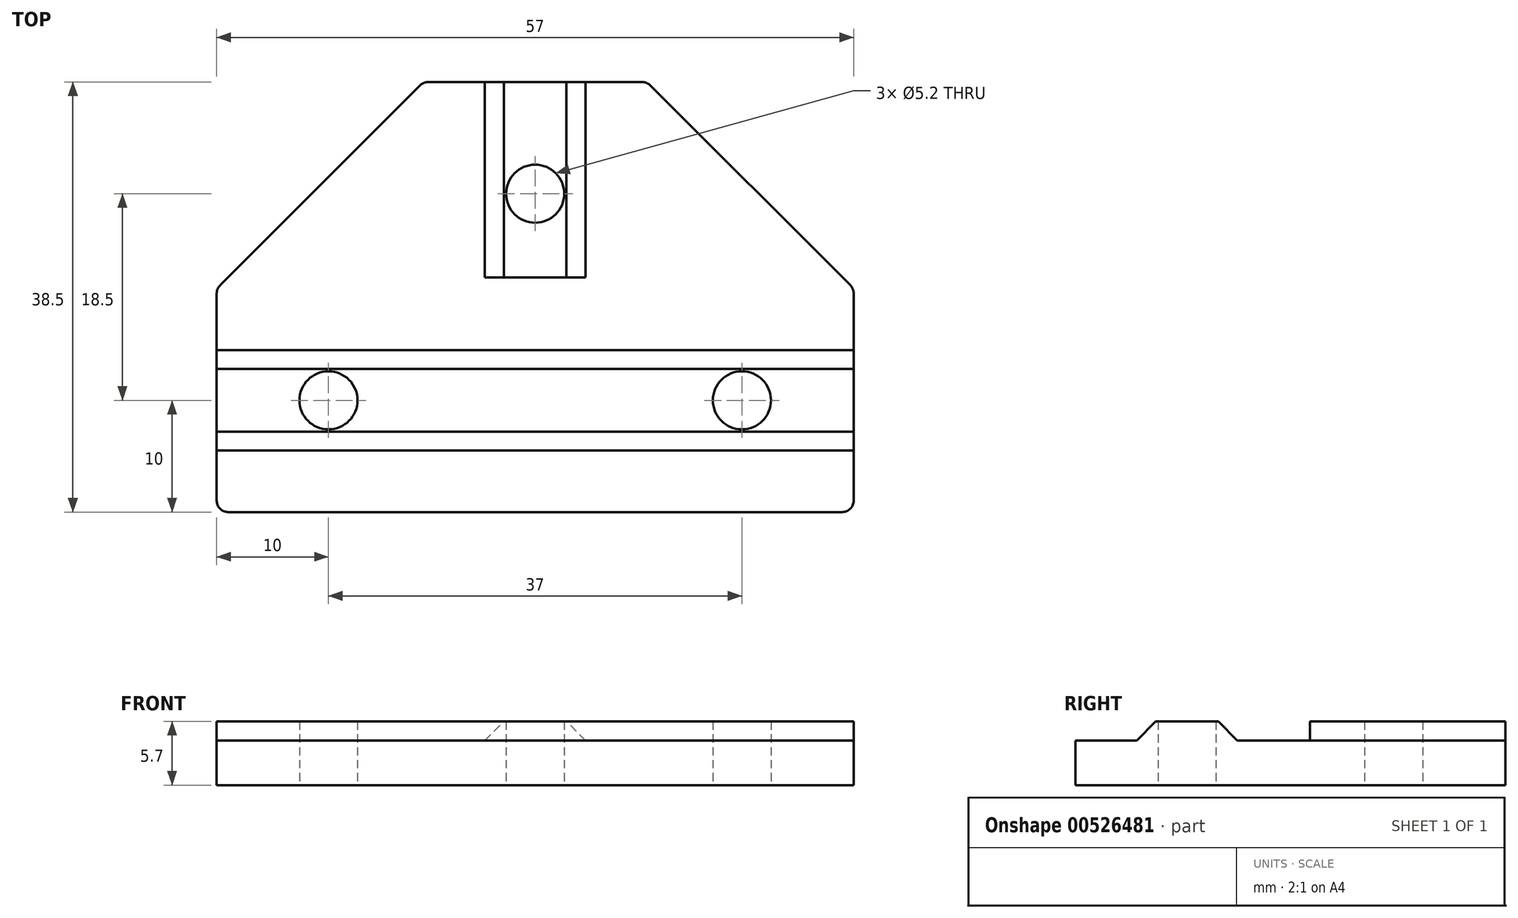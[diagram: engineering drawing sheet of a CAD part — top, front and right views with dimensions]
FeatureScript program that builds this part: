
annotation { "Feature Type Name" : "Feature", "Feature Type Description" : "" }
export const myFeature = defineFeature(function(context is Context, id is Id, definition is map)
    precondition{}
    {
        {
            var Q0;
            Q0=qCreatedBy(makeId("Top.planeOp"),FACE);
            var sketch = newSketch(context, id + "F0", { "sketchPlane" : qUnion([Q0])});
            skLineSegment(sketch, "E0", {"start": v(0, 0) * mm, "end": v(-28.5, 0) * mm});
            skLineSegment(sketch, "E1", {"start": v(-28.5, 0) * mm, "end": v(-28.5, 20) * mm});
            skLineSegment(sketch, "E2", {"start": v(0, 38.5) * mm, "end": v(0, 31.1) * mm});
            skCircle(sketch, "E3", {"center": v(-18.5, 10) * mm, "radius": 2.6 * mm});
            skArc(sketch, "E4", {"start": v(0, 31.1) * mm, "mid": v(-2.6, 28.5) * mm, "end": v(0, 25.9) * mm});
            skLineSegment(sketch, "E5", {"start": v(0, 38.5) * mm, "end": v(-10, 38.5) * mm});
            skLineSegment(sketch, "E6", {"start": v(-10, 38.5) * mm, "end": v(-28.5, 20) * mm});
            skLineSegment(sketch, "E7.trimOffspring", {"start": v(0, 25.9) * mm, "end": v(0, 0) * mm});
            skSolve(sketch);
        }
        {
            var Q0;
            Q0 = qSketchRegion(id + "F0", true);
            extrude(context, id + "F1", {"entities" : qUnion([Q0]), "depth" : 4 * mm, "offsetDistance" : 25 * mm});
        }
        {
            var Q0;
            Q0=makeQuery(id+"F1.opExtrude","CAP_FACE",FACE,{"disambiguationData":[OSD([sQuery(id+"F0.wireOp",EDGE,"E0"),sQuery(id+"F0.wireOp",EDGE,"E1"),sQuery(id+"F0.wireOp",EDGE,"E2"),sQuery(id+"F0.wireOp",EDGE,"E3"),sQuery(id+"F0.wireOp",EDGE,"E4"),sQuery(id+"F0.wireOp",EDGE,"E5"),sQuery(id+"F0.wireOp",EDGE,"E6"),sQuery(id+"F0.wireOp",EDGE,"E7.trimOffspring")])],"isStart":false});
            var sketch = newSketch(context, id + "F2", { "sketchPlane" : qUnion([Q0])});
            skLineSegment(sketch, "E8.bottom", {"start": v(-28.5, 14.5) * mm, "end": v(0, 14.5) * mm});
            skLineSegment(sketch, "E8.top", {"start": v(-28.5, 5.5) * mm, "end": v(0, 5.5) * mm});
            skLineSegment(sketch, "E8.left", {"start": v(-28.5, 14.5) * mm, "end": v(-28.5, 5.5) * mm});
            skLineSegment(sketch, "E8.right", {"start": v(0, 14.5) * mm, "end": v(0, 5.5) * mm});
            skCircle(sketch, "E9.0", {"center": v(-18.5, 10) * mm, "radius": 2.6 * mm});
            skArc(sketch, "E10.0", {"start": v(0, 31.1) * mm, "mid": v(-2.6, 28.5) * mm, "end": v(0, 25.9) * mm});
            skLineSegment(sketch, "E11", {"start": v(0, 38.5) * mm, "end": v(-4.5, 38.5) * mm});
            skLineSegment(sketch, "E12", {"start": v(-4.5, 38.5) * mm, "end": v(-4.5, 21) * mm});
            skLineSegment(sketch, "E13", {"start": v(-4.5, 21) * mm, "end": v(0, 21) * mm});
            skLineSegment(sketch, "E14", {"start": v(0, 25.9) * mm, "end": v(0, 21) * mm});
            skLineSegment(sketch, "E15", {"start": v(0, 38.5) * mm, "end": v(0, 31.1) * mm});
            skSolve(sketch);
        }
        {
            var Q0;
            Q0 = qSketchRegion(id + "F2", true);
            extrude(context, id + "F3", {"entities" : qUnion([Q0]), "operationType" : NewBodyOperationType.ADD, "depth" : 1.7 * mm, "offsetDistance" : 25 * mm});
        }
        {
            var Q0;
            Q0=makeQuery(id+"F3.opExtrude","CAP_EDGE",EDGE,{"disambiguationData":[OSD([sQuery(id+"F2.wireOp",EDGE,"E8.bottom")])],"isStart":false});
            var Q1;
            Q1=makeQuery(id+"F3.opExtrude","CAP_EDGE",EDGE,{"disambiguationData":[OSD([sQuery(id+"F2.wireOp",EDGE,"E8.top")])],"isStart":false});
            var Q2;
            Q2=makeQuery(id+"F3.opExtrude","CAP_EDGE",EDGE,{"disambiguationData":[OSD([sQuery(id+"F2.wireOp",EDGE,"E12")])],"isStart":false});
            chamfer(context, id + "F4", {"entities" : qUnion([Q0, Q1, Q2]), "width" : 1.7 * mm, "tangentPropagation" : true});
        }
        {
            var Q0;
            Q0=makeQuery(id+"F1.opExtrude","SWEPT_EDGE",EDGE,{"disambiguationData":[OSD([sQuery(id+"F0.wireOp",EDGE,"E5"),sQuery(id+"F0.wireOp",EDGE,"E6")])]});
            var Q1;
            Q1=makeQuery(id+"F1.opExtrude","SWEPT_EDGE",EDGE,{"disambiguationData":[OSD([sQuery(id+"F0.wireOp",EDGE,"E1"),sQuery(id+"F0.wireOp",EDGE,"E6")])]});
            var Q2;
            Q2=makeQuery(id+"F1.opExtrude","SWEPT_EDGE",EDGE,{"disambiguationData":[OSD([sQuery(id+"F0.wireOp",EDGE,"E0"),sQuery(id+"F0.wireOp",EDGE,"E1")])]});
            fillet(context, id + "F5", {"entities" : qUnion([Q0, Q1, Q2]), "radius" : 1 * mm, "tangentPropagation" : true, "allowEdgeOverflow" : false});
        }
        {
            var Q0;
            Q0=makeQuery(id+"F1.opExtrude","SWEPT_BODY",BODY,{"disambiguationData":[OSD([sQuery(id+"F0.wireOp",EDGE,"E0"),sQuery(id+"F0.wireOp",EDGE,"E1"),sQuery(id+"F0.wireOp",EDGE,"E2"),sQuery(id+"F0.wireOp",EDGE,"E3"),sQuery(id+"F0.wireOp",EDGE,"E4"),sQuery(id+"F0.wireOp",EDGE,"E5"),sQuery(id+"F0.wireOp",EDGE,"E6"),sQuery(id+"F0.wireOp",EDGE,"E7.trimOffspring")])]});
            var Q1;
            Q1=makeQuery(id+"F3.boolean.opBoolean","MERGE",FACE,{"derivedFrom":[makeQuery(id+"F1.opExtrude","SWEPT_FACE",FACE,{"disambiguationData":[OSD([sQuery(id+"F0.wireOp",EDGE,"E2")])]}),makeQuery(id+"F3.opExtrude","SWEPT_FACE",FACE,{"disambiguationData":[OSD([sQuery(id+"F2.wireOp",EDGE,"E15")])]})]});
            mirror(context, id + "F6", {"operationType" : NewBodyOperationType.ADD, "entities" : qUnion([Q0]), "mirrorPlane" : qUnion([Q1])});
        }
    });
